# Revit family: Deca_Ducha higiênica com registro_Aspen_1984.35.ACT
name_source: partatom
category: Plumbing Fixtures
units: mm (PartAtom-declared; Revit-internal decimal feet)

## family parameters
Cut with Voids When Loaded = No
Host = Face
Part Type = Normal
Room Calculation Point = No
Round Connector Dimension = Use Radius
Shared = No

## types (1)
- 1984.C35.ACT_Cromado
    Aprovado por = quattroD
    Atendimento ao Cliente = 0800-0117073
    Categoria = Chuveiros e duchas
    Composição Básica = Liga cobre (bronze e latão);Aço;Plástico de Engenharia;Elastômeros
    Consumo = Otimização do jato de água
    Cor Principal = Cromado
    Criado por = quattroD
    Código Pai = 1984.35.ACT
    Default Elevation = 0.7 m
    Diâmetro Água Fria = 0.02 m
    Linha = Aspen
    Manufacturer = DECA
    Material = Deca_Cromado
    Material Secundário = Deca_Branco
    Model = 1984.C35.ACT
    Norma = NBR14877
    Peso Líquido (Kg) = 0.704
    Raio Água Fria = 0.01 m
    Segmento = Banheiro Competitivo (D41)
    Tipo de dispositivo economizador = Sim
    Tipo de mecanismo utilizado = MVC -1/4 volta
    Tipo de rosca de entrada = BSP NBR 8133
    URL = www.deca.com.br
    Vazão na Pressão máx. (L/min) = 6
    Vazão na Pressão mín. (L/min) = 4

## geometry (parser evidence)
native form markers: Sweep x2
no freeform markers — native parametric forms only
